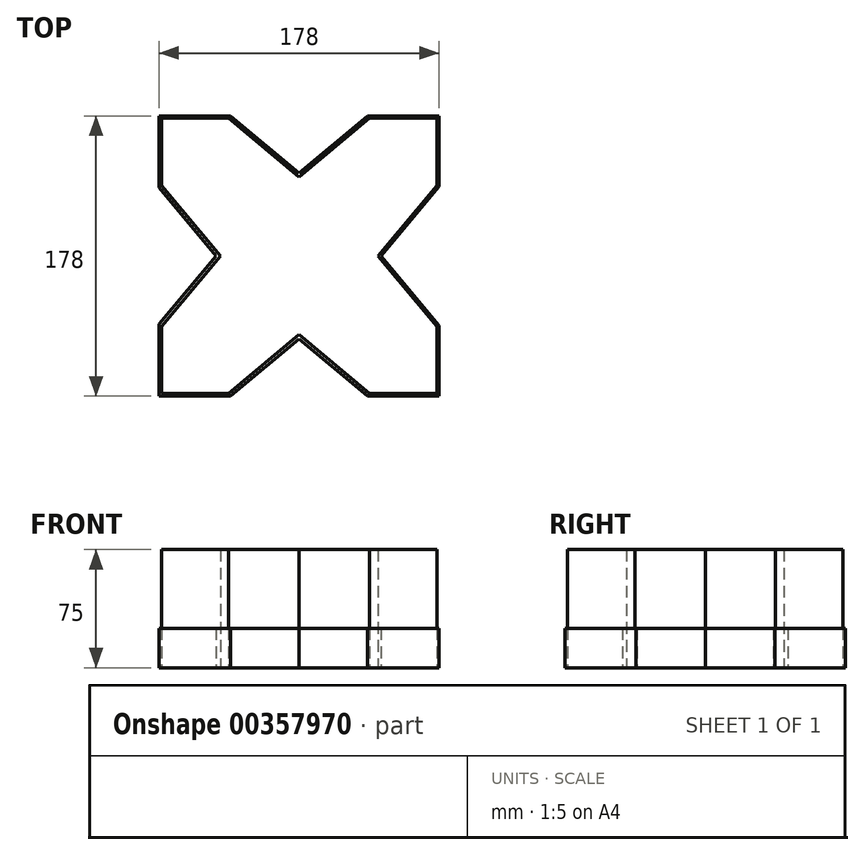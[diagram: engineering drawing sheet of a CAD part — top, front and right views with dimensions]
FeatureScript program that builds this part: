
annotation { "Feature Type Name" : "Feature", "Feature Type Description" : "" }
export const myFeature = defineFeature(function(context is Context, id is Id, definition is map)
    precondition{}
    {
        {
            var Q0;
            Q0=qCreatedBy(makeId("Top.planeOp"),FACE);
            var sketch = newSketch(context, id + "F0", { "sketchPlane" : qUnion([Q0])});
            skLineSegment(sketch, "E0.bottom", {"start": v(87.5, 87.5) * mm, "end": v(-87.5, 87.5) * mm});
            skLineSegment(sketch, "E0.top", {"start": v(87.5, -87.5) * mm, "end": v(-87.5, -87.5) * mm});
            skLineSegment(sketch, "E0.left", {"start": v(87.5, 87.5) * mm, "end": v(87.5, -87.5) * mm});
            skLineSegment(sketch, "E0.right", {"start": v(-87.5, 87.5) * mm, "end": v(-87.5, -87.5) * mm});
            skPoint(sketch, "E0.middle", {"position": v(0, 0) * mm});
            skLineSegment(sketch, "E1", {"start": v(-44.7, 87.5) * mm, "end": v(0, 50) * mm});
            skLineSegment(sketch, "E2", {"start": v(0, 50) * mm, "end": v(44.7, 87.5) * mm});
            skLineSegment(sketch, "E3", {"start": v(50, 0) * mm, "end": v(87.5, 44.7) * mm});
            skLineSegment(sketch, "E4", {"start": v(50, 0) * mm, "end": v(87.5, -44.7) * mm});
            skLineSegment(sketch, "E5", {"start": v(44.7, -87.5) * mm, "end": v(0, -50) * mm});
            skLineSegment(sketch, "E6", {"start": v(0, -50) * mm, "end": v(-44.7, -87.5) * mm});
            skLineSegment(sketch, "E7", {"start": v(-87.5, -44.7) * mm, "end": v(-50, 0) * mm});
            skLineSegment(sketch, "E8", {"start": v(-50, 0) * mm, "end": v(-87.5, 44.7) * mm});
            skLineSegment(sketch, "E9.0", {"start": v(0, 52.61) * mm, "end": v(43.37, 89) * mm});
            skLineSegment(sketch, "E9.1", {"start": v(-43.37, 89) * mm, "end": v(0, 52.61) * mm});
            skLineSegment(sketch, "E10.0", {"start": v(51.96, 0) * mm, "end": v(89, 44.14) * mm});
            skLineSegment(sketch, "E10.1", {"start": v(51.96, 0) * mm, "end": v(89, -44.14) * mm});
            skLineSegment(sketch, "E11.0", {"start": v(-52.61, 0) * mm, "end": v(-89, 43.37) * mm});
            skLineSegment(sketch, "E11.1", {"start": v(-89, -43.37) * mm, "end": v(-52.61, 0) * mm});
            skLineSegment(sketch, "E12.0", {"start": v(89, 89) * mm, "end": v(-89, 89) * mm});
            skLineSegment(sketch, "E12.1", {"start": v(89, 89) * mm, "end": v(89, -89) * mm});
            skLineSegment(sketch, "E12.2", {"start": v(89, -89) * mm, "end": v(-89, -89) * mm});
            skLineSegment(sketch, "E12.3", {"start": v(-89, 89) * mm, "end": v(-89, -89) * mm});
            skLineSegment(sketch, "E13.0", {"start": v(0, -52.61) * mm, "end": v(-43.37, -89) * mm});
            skLineSegment(sketch, "E13.1", {"start": v(43.37, -89) * mm, "end": v(0, -52.61) * mm});
            skSolve(sketch);
        }
        {
            var Q0;
            {var subQ0=sQuery(id+"F0.wireOp",EDGE,"E1");Q0=makeQuery(id+"F0.imprint","IMPRINT",FACE,{"disambiguationData":[TD([[makeQuery(id+"F0.imprint","IMPRINT",EDGE,{"derivedFrom":subQ0}),-1.0]])]});}
            extrude(context, id + "F1", {"entities" : qUnion([Q0]), "depth" : 75 * mm});
        }
        {
            var Q0;
            {var subQ4=sQuery(id+"F0.wireOp",EDGE,"E0.bottom");var subQ6=makeQuery(id+"F0.imprint","INTERSECT",VERTEX,{"derivedFrom":[subQ4,sQuery(id+"F0.wireOp",EDGE,"E1")]});Q0=makeQuery(id+"F0.imprint","IMPRINT",FACE,{"disambiguationData":[TD([[makeQuery(id+"F0.imprint","IMPRINT",EDGE,{"disambiguationData":[TD([[subQ6,1.0]])],"derivedFrom":subQ4}),-1.0]])]});}
            var Q1;
            {var subQ0=sQuery(id+"F0.wireOp",EDGE,"E1");Q1=makeQuery(id+"F0.imprint","IMPRINT",FACE,{"disambiguationData":[TD([[makeQuery(id+"F0.imprint","IMPRINT",EDGE,{"derivedFrom":subQ0}),1.0]])]});}
            var Q2;
            {var subQ4=sQuery(id+"F0.wireOp",EDGE,"E7");Q2=makeQuery(id+"F0.imprint","IMPRINT",FACE,{"disambiguationData":[TD([[makeQuery(id+"F0.imprint","IMPRINT",EDGE,{"derivedFrom":subQ4}),1.0]])]});}
            var Q3;
            {var subQ0=sQuery(id+"F0.wireOp",EDGE,"E0.left");var subQ4=sQuery(id+"F0.wireOp",EDGE,"E0.bottom");var subQ5=makeQuery(id+"F0.imprint","INTERSECT",VERTEX,{"derivedFrom":[subQ4,subQ0]});Q3=makeQuery(id+"F0.imprint","IMPRINT",FACE,{"disambiguationData":[TD([[makeQuery(id+"F0.imprint","IMPRINT",EDGE,{"disambiguationData":[TD([[subQ5,-1.0]])],"derivedFrom":subQ4}),-1.0]])]});}
            var Q4;
            {var subQ0=sQuery(id+"F0.wireOp",EDGE,"E3");Q4=makeQuery(id+"F0.imprint","IMPRINT",FACE,{"disambiguationData":[TD([[makeQuery(id+"F0.imprint","IMPRINT",EDGE,{"derivedFrom":subQ0}),-1.0]])]});}
            var Q5;
            {var subQ6=sQuery(id+"F0.wireOp",EDGE,"E5");Q5=makeQuery(id+"F0.imprint","IMPRINT",FACE,{"disambiguationData":[TD([[makeQuery(id+"F0.imprint","IMPRINT",EDGE,{"derivedFrom":subQ6}),-1.0]])]});}
            var Q6;
            {var subQ3=sQuery(id+"F0.wireOp",EDGE,"E0.top");var subQ5=sQuery(id+"F0.wireOp",EDGE,"E0.right");var subQ9=makeQuery(id+"F0.imprint","INTERSECT",VERTEX,{"derivedFrom":[subQ3,subQ5]});Q6=makeQuery(id+"F0.imprint","IMPRINT",FACE,{"disambiguationData":[TD([[makeQuery(id+"F0.imprint","IMPRINT",EDGE,{"disambiguationData":[TD([[subQ9,1.0]])],"derivedFrom":subQ3}),1.0]])]});}
            var Q7;
            {var subQ0=sQuery(id+"F0.wireOp",EDGE,"E0.left");var subQ1=sQuery(id+"F0.wireOp",EDGE,"E0.top");var subQ2=makeQuery(id+"F0.imprint","INTERSECT",VERTEX,{"derivedFrom":[subQ1,subQ0]});Q7=makeQuery(id+"F0.imprint","IMPRINT",FACE,{"disambiguationData":[TD([[makeQuery(id+"F0.imprint","IMPRINT",EDGE,{"disambiguationData":[TD([[subQ2,-1.0]])],"derivedFrom":subQ1}),1.0]])]});}
            var Q8;
            {var subQ1=sQuery(id+"F0.wireOp",EDGE,"E5");Q8=makeQuery(id+"F0.imprint","IMPRINT",FACE,{"disambiguationData":[TD([[makeQuery(id+"F0.imprint","IMPRINT",EDGE,{"derivedFrom":subQ1}),1.0]])]});}
            extrude(context, id + "F2", {"entities" : qUnion([Q0, Q1, Q2, Q3, Q4, Q5, Q6, Q7, Q8]), "depth" : 25 * mm});
        }
    });
